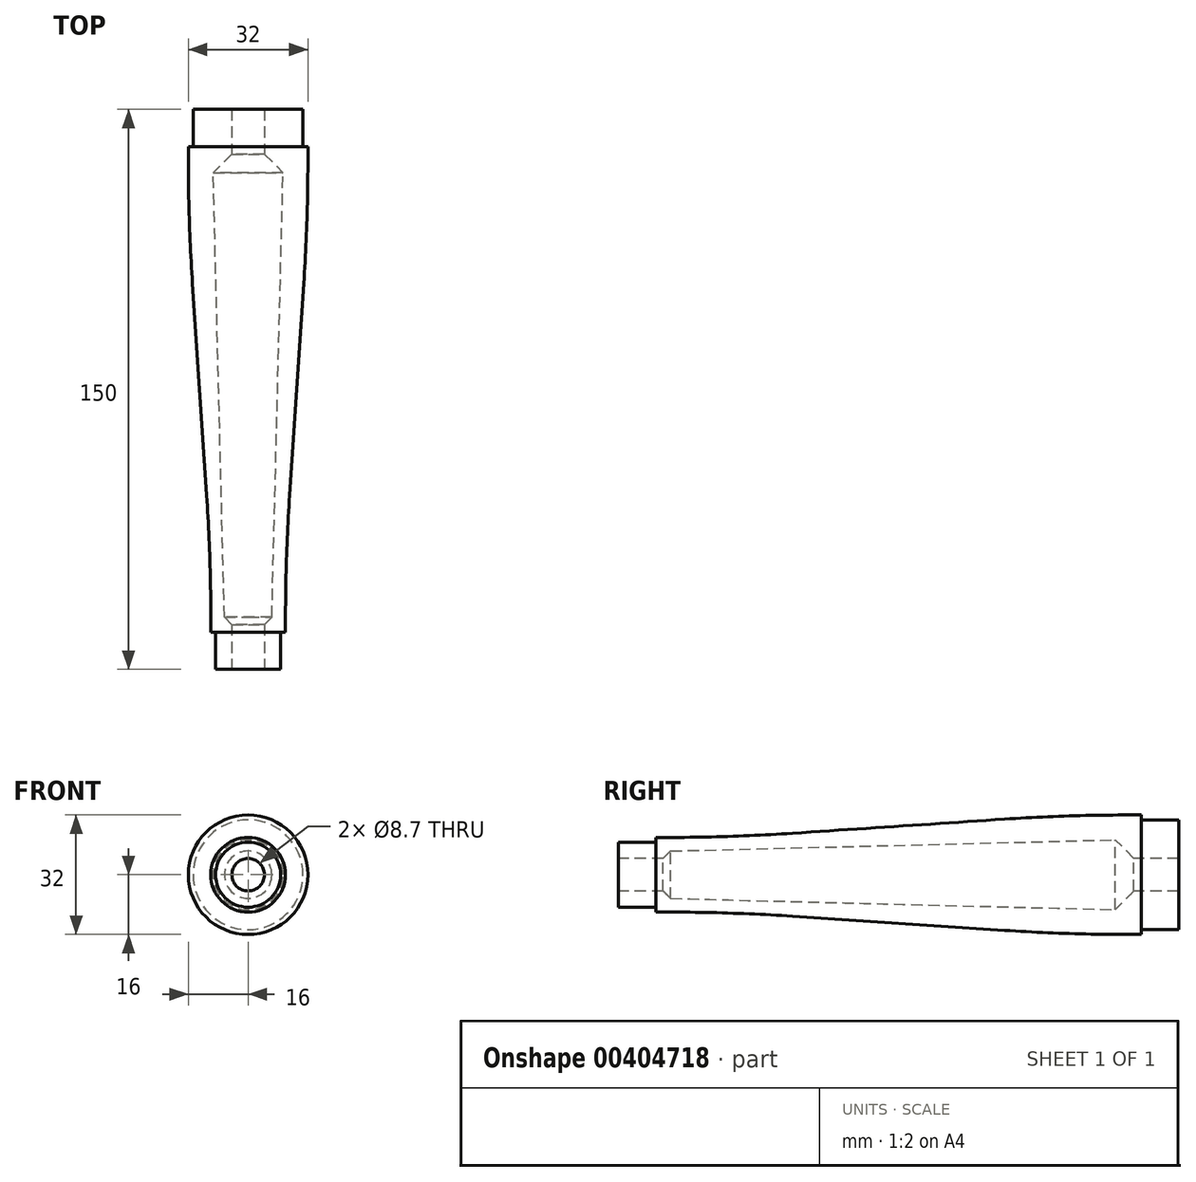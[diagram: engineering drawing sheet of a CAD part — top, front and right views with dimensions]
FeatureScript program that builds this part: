
annotation { "Feature Type Name" : "Feature", "Feature Type Description" : "" }
export const myFeature = defineFeature(function(context is Context, id is Id, definition is map)
    precondition{}
    {
        {
            var Q0;
            Q0=qCreatedBy(makeId("Top.planeOp"),FACE);
            var sketch = newSketch(context, id + "F0", { "sketchPlane" : qUnion([Q0])});
            skLineSegment(sketch, "E0", {"start": v(0, 0) * mm, "end": v(14.7, 0) * mm});
            skLineSegment(sketch, "E1", {"start": v(14.7, 0) * mm, "end": v(14.7, -10) * mm});
            skLineSegment(sketch, "E2", {"start": v(14.7, -10) * mm, "end": v(16, -10) * mm});
            skLineSegment(sketch, "E3", {"start": v(16, -10) * mm, "end": v(16, -30) * mm});
            skLineSegment(sketch, "E4", {"start": v(16, -30) * mm, "end": v(10, -120) * mm});
            skLineSegment(sketch, "E5", {"start": v(10, -120) * mm, "end": v(10, -140) * mm});
            skLineSegment(sketch, "E6", {"start": v(10, -140) * mm, "end": v(8.7, -140) * mm});
            skLineSegment(sketch, "E7", {"start": v(8.7, -140) * mm, "end": v(8.7, -150) * mm});
            skLineSegment(sketch, "E8", {"start": v(8.7, -150) * mm, "end": v(0, -150) * mm});
            skLineSegment(sketch, "E9", {"start": v(0, -150) * mm, "end": v(0, 0) * mm});
            skLineSegment(sketch, "E10", {"start": v(4.35, -150) * mm, "end": v(4.35, -138) * mm});
            skLineSegment(sketch, "E11", {"start": v(4.35, -138) * mm, "end": v(6.35, -136) * mm});
            skLineSegment(sketch, "E12", {"start": v(9.35, -17) * mm, "end": v(4.35, -12) * mm});
            skLineSegment(sketch, "E13", {"start": v(4.35, -12) * mm, "end": v(4.35, 0) * mm});
            skLineSegment(sketch, "E14", {"start": v(6.35, -136) * mm, "end": v(9.35, -17) * mm});
            skSolve(sketch);
        }
        {
            var Q0;
            {var subQ0=sQuery(id+"F0.wireOp",EDGE,"E1");Q0=makeQuery(id+"F0.imprint","IMPRINT",FACE,{"disambiguationData":[TD([[makeQuery(id+"F0.imprint","IMPRINT",EDGE,{"derivedFrom":subQ0}),-1.0]])]});}
            var Q1;
            Q1=sQuery(id+"F0.wireOp",EDGE,"E9");
            revolve(context, id + "F1", {"entities" : qUnion([Q0]), "axis" : qUnion([Q1]), "revolveType" : RevolveType.FULL});
        }
        {
            var Q0;
            Q0=makeQuery(id+"F1.opRevolve","SWEPT_EDGE",EDGE,{"disambiguationData":[OSD([sQuery(id+"F0.wireOp",EDGE,"E3"),sQuery(id+"F0.wireOp",EDGE,"E4")])]});
            var Q1;
            Q1=makeQuery(id+"F1.opRevolve","SWEPT_EDGE",EDGE,{"disambiguationData":[OSD([sQuery(id+"F0.wireOp",EDGE,"E4"),sQuery(id+"F0.wireOp",EDGE,"E5")])]});
            fillet(context, id + "F2", {"entities" : qUnion([Q0, Q1]), "radius" : 500 * mm, "tangentPropagation" : true, "allowEdgeOverflow" : false});
        }
    });
